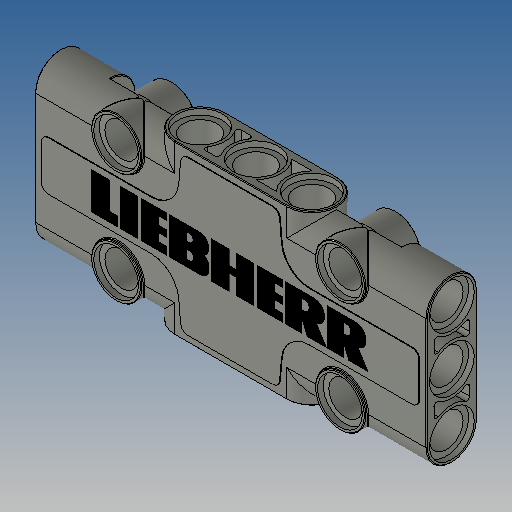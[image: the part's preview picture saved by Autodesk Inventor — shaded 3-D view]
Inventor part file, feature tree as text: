
AUTODESK INVENTOR PART (.ipt)
format: ipt  version: 2025 (Build 290162010, 162A)  size: 1,231,360 bytes
history: native  units: in
note: dims shown in document units (in); Inventor stores cm internally (conversion verified against a paired STEP export)
features: extrude x17, sketch x13, mirror x5, other x2, plane x1, fillet x1
ambient origin geometry x8: Origin, YZ Plane, XZ Plane, XY Plane, X Axis, Y Axis, Z Axis, Center Point
bodies: Solid1 (feature_tree)
feature tree (39):
  extrude  "Extrusion1"  Depth=0.189in
  sketch  "Sketch3"  dims[d4=2.2047in d5=0.0in]
  extrude  "Extrusion2"  Depth=0.0315in
  extrude  "Extrusion3"  TaperAngle=0.0deg  [1 undecoded]
  extrude  "Extrusion4"  Depth=0.252in
  plane  "Work Plane1"
  extrude  "Extrusion5"  Depth=0.7874in
  sketch  "Sketch5"  dims[d12=0.3937in d14=0.3937in d16=0.2835in]
  extrude  "Extrusion6"  Depth=0.3937in
  extrude  "Extrusion7"  Depth=0.0315in
  extrude  "Extrusion10"  Depth=0.2205in TaperAngle=0.0deg
  extrude  "Extrusion8"  Depth=0.189in
  extrude  "Extrusion9"  Depth=0.0315in TaperAngle=0.0deg
  mirror  "Mirror1"
  mirror  "Mirror2"
  sketch  "Sketch8"  dims[d22=-0.1417in d23=0.189in]
  extrude  "Extrusion11"  Depth=0.189in
  extrude  "Extrusion12"  Depth=0.2677in
  extrude  "Extrusion13"  Depth=0.0039in TaperAngle=0.0deg
  sketch  "Sketch9"  dims[d24=0.2835in d25=0.0315in d26=0.0in]
  extrude  "Extrusion14"  Depth=0.0039in
  extrude  "Extrusion16"  Depth=0.0039in
  mirror  "Mirror3"
  extrude  "Extrusion15"  TaperAngle=0.0deg  [1 undecoded]
  fillet  "Fillet1"  Radius=0.252in
  extrude  "Extrusion17"  Depth=0.0039in
  mirror  "Spiegeln4"
  mirror  "Spiegeln5"
  other  "Aufkleber1"
  sketch  "Sketch2"  dims[d2=0.2835in d3=0.0315in]
  sketch  "Skizze - Rechteckige Anordnung1"  dims[d0=0.315in d1=0.189in]
  sketch  "Sketch4"  dims[d8=45.0deg d9=0.7874in d11=0.315in]
  sketch  "Sketch6"  dims[d17=0.0in d18=0.0315in]
  sketch  "Sketch7"  dims[d19=0.0in d20=0.2205in d21=0.0in]
  sketch  "Sketch10"  dims[d27=0.2835in d28=0.189in]
  sketch  "Skizze - Rechteckige Anordnung3"  dims[d6=0.189in d7=0.252in]
  sketch  "Skizze11"  dims[d29=0.6299in d30=0.2677in d31=0.0472in]
  sketch  "Skizze12"  dims[d32=0.0in d33=0.0in d34=0.2677in d35=0.0in d36=0.252in d37=0.0315in d38=0.0in d39=0.252in d40=0.0315in d41=0.0in d42=0.0315in d43=0.2205in d44=0.0in d45=0.2835in d46=0.6299in d47=0.189in d48=0.1417in d49=0.1417in d50=0.0in d51=0.0in d52=0.1417in d53=0.0in d54=0.315in d55=0.0in d56=0.252in d57=0.0315in d58=0.0in d59=1.5748in d60=0.126in d62=0.0079in d63=0.0in d64=45.0deg d72=0.2205in d73=0.0in d74=0.0039in d75=0.0157in d76=0.7874in d78=0.315in d79=0.3937in d81=0.3937in d83=0.1378in d84=0.1575in d85=0.8268in d86=0.0394in d87=0.0394in d88=0.6528in d89=0.0394in d90=0.0039in d91=0.0in]
  other  "Bild1"
note: 2 required parameter values undecoded (feature->parameter linkage not recoverable at this tier; creation-order binding heuristic only, values carry confidence <= 0.55)
